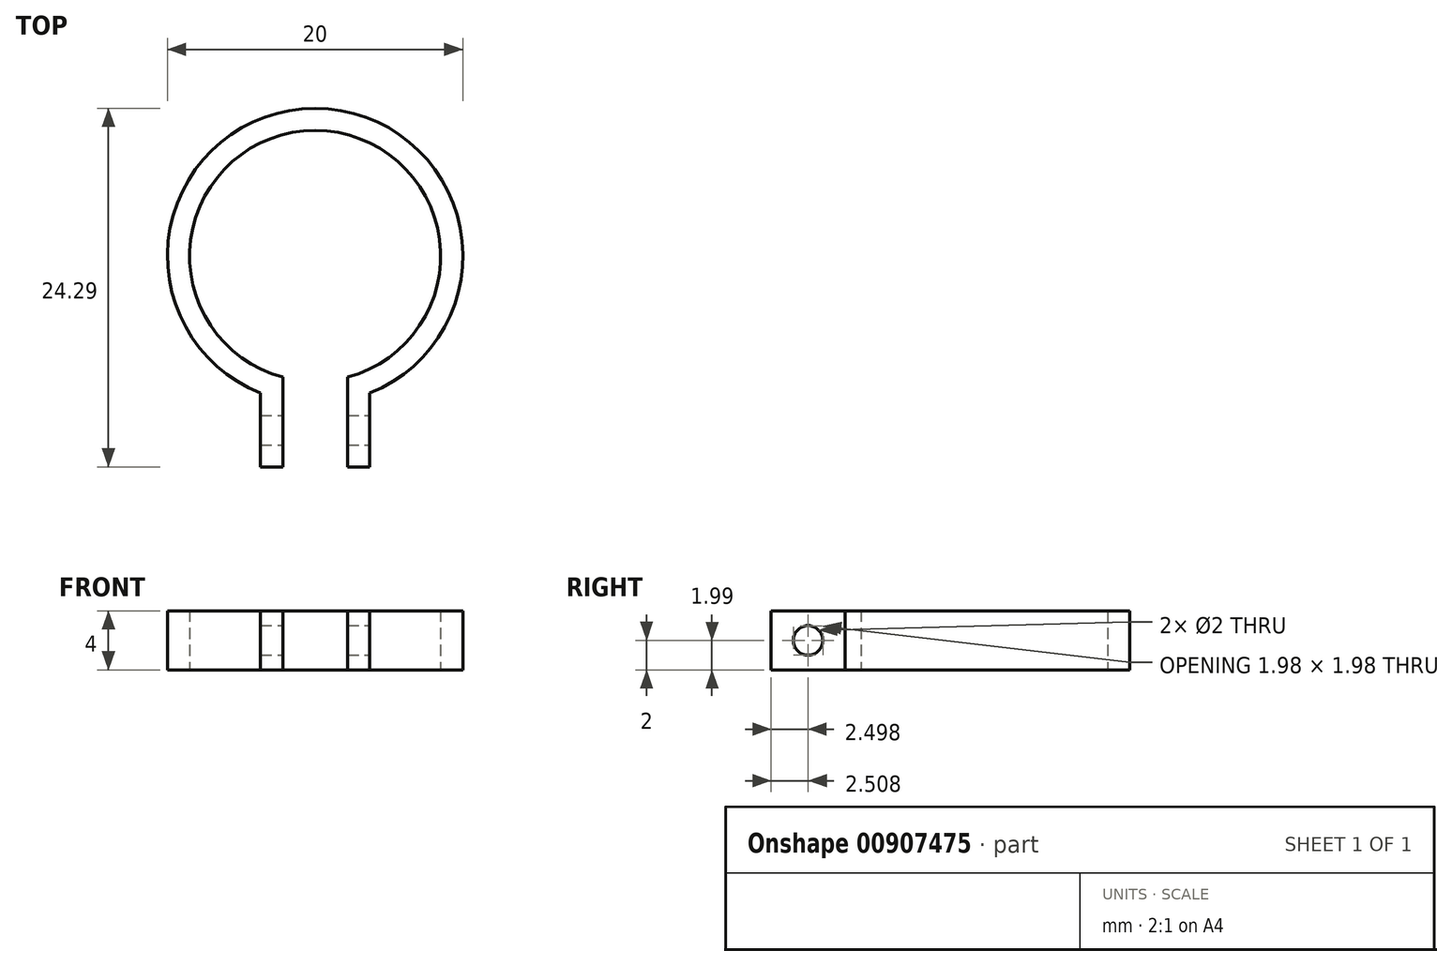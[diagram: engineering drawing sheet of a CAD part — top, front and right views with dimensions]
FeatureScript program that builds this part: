
annotation { "Feature Type Name" : "Feature", "Feature Type Description" : "" }
export const myFeature = defineFeature(function(context is Context, id is Id, definition is map)
    precondition{}
    {
        {
            var Q0;
            Q0=qCreatedBy(makeId("Top.planeOp"),FACE);
            var sketch = newSketch(context, id + "F0", { "sketchPlane" : qUnion([Q0])});
            skLineSegment(sketch, "E0.top", {"start": v(3.7, -14.3) * mm, "end": v(2.2, -14.3) * mm});
            skPoint(sketch, "E0.middle", {"position": v(0, -10) * mm});
            skLineSegment(sketch, "E1", {"start": v(2.2, -8.21) * mm, "end": v(2.2, -9.76) * mm});
            skLineSegment(sketch, "E2", {"start": v(3.7, -9.3) * mm, "end": v(3.7, -14.3) * mm});
            skLineSegment(sketch, "E3", {"start": v(2.2, -9.76) * mm, "end": v(2.2, -14.3) * mm});
            skLineSegment(sketch, "E4", {"start": v(-2.2, -8.21) * mm, "end": v(-2.2, -9.76) * mm});
            skLineSegment(sketch, "E5", {"start": v(-2.2, -9.76) * mm, "end": v(-2.2, -14.3) * mm});
            skLineSegment(sketch, "E6", {"start": v(-3.7, -9.3) * mm, "end": v(-3.7, -14.3) * mm});
            skLineSegment(sketch, "E7", {"start": v(-2.2, -14.3) * mm, "end": v(-3.7, -14.3) * mm});
            skArc(sketch, "E8", {"start": v(2.2, -8.21) * mm, "mid": v(0, 8.5) * mm, "end": v(-2.2, -8.21) * mm});
            skArc(sketch, "E9", {"start": v(3.7, -9.3) * mm, "mid": v(0, 10) * mm, "end": v(-3.7, -9.3) * mm});
            skSolve(sketch);
        }
        {
            var Q0;
            Q0 = qSketchRegion(id + "F0", true);
            extrude(context, id + "F1", {"entities" : qUnion([Q0]), "depth" : 4 * mm, "offsetDistance" : 25 * mm});
        }
        {
            var Q0;
            Q0=makeQuery(id+"F1.opExtrude","SWEPT_FACE",FACE,{"disambiguationData":[OSD([sQuery(id+"F0.wireOp",EDGE,"E2")])]});
            var sketch = newSketch(context, id + "F2", { "sketchPlane" : qUnion([Q0])});
            skCircle(sketch, "E10", {"center": v(-11.8, 2) * mm, "radius": 1 * mm});
            skPoint(sketch, "E10.centerSnap0", {"position": v(-9.3, 2) * mm});
            skPoint(sketch, "E10.centerSnap1", {"position": v(-11.8, 4) * mm});
            skSolve(sketch);
        }
        {
            var Q0;
            Q0=makeQuery(id+"F2.imprint","IMPRINT",FACE,{"disambiguationData":[TD([[makeQuery(id+"F2.imprint","IMPRINT",EDGE,{"derivedFrom":sQuery(id+"F2.wireOp",EDGE,"E10")}),1.0]])]});
            extrude(context, id + "F3", {"entities" : qUnion([Q0]), "operationType" : NewBodyOperationType.REMOVE, "oppositeDirection" : true, "depth" : 25 * mm, "offsetDistance" : 25 * mm});
        }
    });
